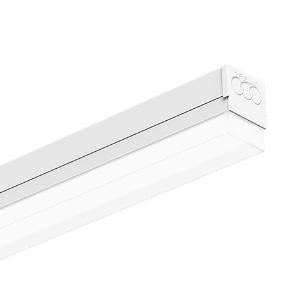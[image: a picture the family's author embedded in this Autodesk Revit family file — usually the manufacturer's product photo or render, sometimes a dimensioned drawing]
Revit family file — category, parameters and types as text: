
# Revit family: 3f_filippi_-_3f_linux_dr_3f_filippi_-_a20512_-_3f_linux_dr_2x22_led_l1778
name_source: partatom
category: Lighting Fixtures
units: mm (PartAtom-declared; Revit-internal decimal feet)

## family parameters
Cut with Voids When Loaded = No
Host = Face
Light Source = No
Part Type = Normal
Room Calculation Point = No
Round Connector Dimension = Use Diameter
Shared = No

## types (1)
- 3F Filippi - 3F Linux DR (1 x LED, 6253 lm, 49 W, 4000 K)
    Apparent Load = 49 VA
    Approval mark = CE
    CIE Flux Codes = 41 72 91 86 100
    Color Rendering = 80
    Color Temperature = 4000 K
    Control Gear = Electronic ballast
    Default Elevation = 1800 mm
    Description = Light unit for structure continues 3F Linux S.

ILLUMINOTECHNICAL
Luminous efficiency 100% (DLOR 86%, ULOR 14%).
Initial luminous flux of the luminaire 6253 lm.
Diffused symmetric distribution.
Installation Interdistance Transv.D = 1.38 x hu - Long.D = 1.25 x hu.
Tabular UGR (CIE 117 - 4H-8H; S=0.25H; 70/50/20): RUG 25 - 23.6.
Beam angle: 136° - 112°.
Luminous efficacy 128 lm/W.
Lifetime (L93/B10): 30000 h. (tq+25°C)
Lifetime (L90/B10): 50000 h. (tq+25°C)
Lifetime (L85/B10): 80000 h. (tq+25°C)
Lifetime (L80/B10): 100000 h. (tq+25°C)
Sudden decreased luminous flux after 50000 hours: 0% (C0).
Photobiological safety in compliance with IEC/TR 62778: RG0 risk exempt, (IEC 62471).
In compliance with IEC/EN 62722-2-1 - IEC/EN 62717 standards.

SOURCE
2 linear LED modules 22W/840.
Energy efficiency class (UE 2019/2020 - UE 2019/2015): D.
CIE 13.3 Colour rendering index: CRI >80 (R9 <50%).
IES TM-30 Fidelity Index: Rf = 84 Rg = 95.
CCT nominal colour temperature 4000 K.
Colour initial tolerance (MacAdam): SDCM 3.

MECHANICAL
Light unit in hot-galvanised steel, painted in white polyester base with fixing springs and retractable safety hooks in stainless steel.
Rectangular screen in self-extinguishing polycarbonate, UV stabilised, opal, with smooth outer surface.
Luminaire with limited surface temperature. - D - (EN 60598-2-24)
Dimensions: 1778x62 mm, height 81 mm. Weight 2.425 kg.
IP40 protection degree.
Mechanical strength to impacts IK06 (1 joule).
Glow-wire test resistance 850°C.

ELECTRICAL
Halogen Free electronic wiring 230V-50/60Hz, power factor 0.95, THD <25%, constant output current, SELV, class I, 1 driver.
Power of the luminaire 49 W.
ENEC - CE.
SAFE FLICKER: PstLM=<1 and SVM=<0.4 (IEC TR 61547-1 and IEC TR 63158), to ensure a more comfortable and safe light.
Luminaire compliant with EN 60598-2-22 for power supply from a centralised emergency system CPSS (Central Power Supply System), not incorporated in the luminaire - high risk areas excluded. The default power and flux are 100% in AC and 100% in DC.
Ambient temperature from 0°C to +35°C.
Temperature class T6 max 85°C.
Connection to the structure with 3-pin plug with phase selection (H05Z-U Halogen Free cable section 0.5 mm² HT90).
Relative humidity UR: <85%.

INSTALLATION
Ceiling / Suspended / Wall.
All accessories dedicated to this product are available on the Catalog and on our website www.3F-Filippi.com.

STRUCTURE
Hot-galvanised wired structure, painted in polyester base white, obtained through rolling process.
Saline-mist resistance equal to 300hrs and damp resistance equal to 700hrs.
Through-wiring 5 or 7 poles with cables H07Z-U Halogen Free section 2.5 mm² HT90, with quick connecting terminal, irreversible, start / end and intermediate power towers.
Linear connecting element in hot galvanised steel already mounted on one end to form continuous channels, only L3556 structures.
A20017 - 3F Linux S 5P L3556, structure with through-wiring 5-pole.
A20019 - 3F Linux S 5P L1778, structure with through-wiring 5-pole.
A20024 - 3F Linux S 7P L3556, structure with through-wiring 7-pole.
A20026 - 3F Linux S 7P L1778, structure with through-wiring 7-pole.

APPLICATIONS
Suitable product for food production plants (HACCP), IFS (Food Version 6), BRC (GSFS Food Version 7).
In commercial environments, exhibition areas, shops and stores.

WARNING
Luminaire designed for disposal/recycling at end-of-life.
Replaceable (LED only) light source by a professional. Replaceable control gear by a professional.
    Height = 81 mm
    Lamp = 1 x LED
    Lamp Light Flux = 6253 lm
    Lamp Power = 49 W
    Lamp count = 1
    Length = 1778 mm
    Lifetime = 50000 h
    Luminous efficacy = 128 lm/W
    Manufacturer = 3F Filippi
    ModVariant = No
    Model = 3F Filippi - A20512 - 3F Linux DR 2x22 LED L1778
    Mounting Place = Ceiling
    Mounting Type = Pendant
    Number of Poles = 1
    OnlyDefault = Yes
    Power Factor = 1
    Product Name = 3F Filippi - 3F Linux DR
    Product group = pendant luminaire
    ProductGroupID = 9
    Protection Class = Protection class I
    Protection Degree = IP 40
    RLX_Detail_Level = 1
    RLX_Emergency_Light_Flux = 0 lm
    RLX_Emergency_Type = 0
    RLX_Emergency_Type_DB = No
    RlxData = <blob elided: 33909 chars, md5=12922709>
    Socket = socket
    Standby Power = 0 W
    System Light Flux = 6253 lm
    System Power = 49 W
    Type Comments = Product without accessories
    Type Image = 3ffilippi_3f_linux_dr.jpg
    URL = http://relux.com
    VarID = ---
    Voltage = 0 V
    Weight = 0.00 kg
    Width = 62 mm  [stored 0.203412 ft]

note: [stored X ft] marks values corroborated as IEEE doubles in the binary element streams (Revit-internal decimal feet)

## geometry (parser evidence)
native form markers: Blend x4, Sweep x13
no freeform markers — native parametric forms only
